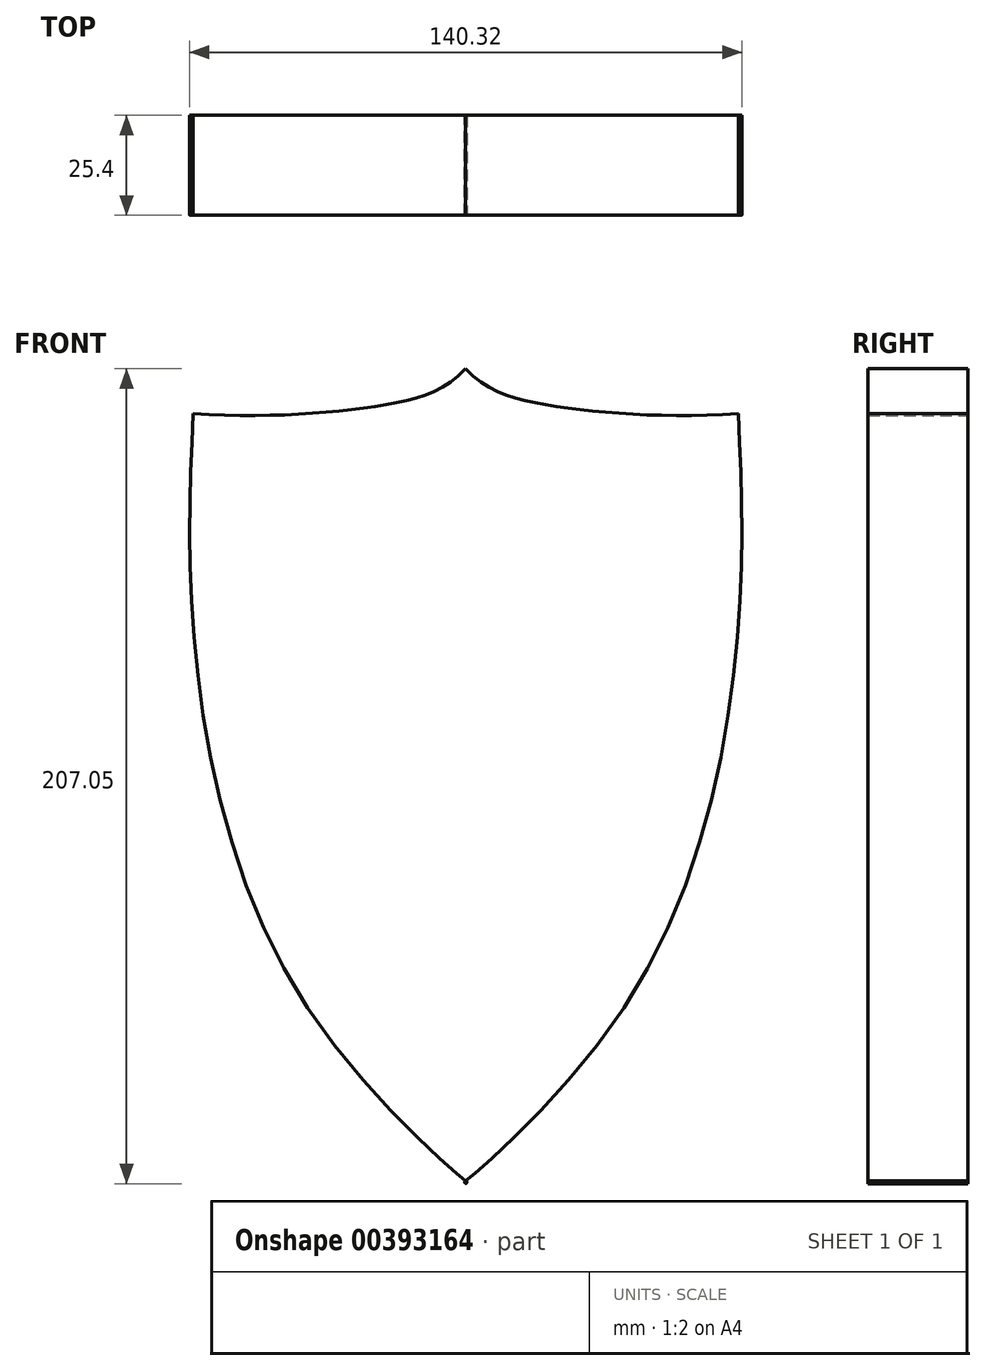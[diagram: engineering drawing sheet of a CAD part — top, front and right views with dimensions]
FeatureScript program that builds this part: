
annotation { "Feature Type Name" : "Feature", "Feature Type Description" : "" }
export const myFeature = defineFeature(function(context is Context, id is Id, definition is map)
    precondition{}
    {
        {
            var Q0;
            Q0=qCreatedBy(makeId("Front.planeOp"),FACE);
            var sketch = newSketch(context, id + "F0", { "sketchPlane" : qUnion([Q0])});
            skLineSegment(sketch, "E0.bottom", {"start": v(245.74, -123.57) * mm, "end": v(1458.6, -123.57) * mm});
            skLineSegment(sketch, "E0.top", {"start": v(239.4, -790.32) * mm, "end": v(1458.6, -790.32) * mm});
            skLineSegment(sketch, "E0.left", {"start": v(239.4, -129.92) * mm, "end": v(239.4, -790.32) * mm});
            skLineSegment(sketch, "E0.right", {"start": v(1458.6, -123.57) * mm, "end": v(1458.6, -790.32) * mm});
            skPoint(sketch, "E1.visualSharp", {"position": v(239.4, -123.57) * mm});
            skArc(sketch, "E1.filletArc", {"start": v(245.74, -123.57) * mm, "mid": v(241.25, -125.43) * mm, "end": v(239.4, -129.92) * mm});
            skLineSegment(sketch, "E2.bottom", {"start": v(331.62, -510.92) * mm, "end": v(1373.02, -510.92) * mm});
            skLineSegment(sketch, "E2.top", {"start": v(331.62, -256.92) * mm, "end": v(1373.02, -256.92) * mm});
            skLineSegment(sketch, "E2.left", {"start": v(331.62, -510.92) * mm, "end": v(331.62, -256.92) * mm});
            skLineSegment(sketch, "E2.right", {"start": v(1373.02, -510.92) * mm, "end": v(1373.02, -256.92) * mm});
            skLineSegment(sketch, "E3", {"start": v(852.32, -256.92) * mm, "end": v(852.32, -510.92) * mm});
            skLineSegment(sketch, "E4", {"start": v(239.4, -460.12) * mm, "end": v(1458.6, -460.12) * mm});
            skLineSegment(sketch, "E5", {"start": v(591.97, -256.92) * mm, "end": v(591.97, -510.92) * mm});
            skLineSegment(sketch, "E6", {"start": v(1112.67, -256.92) * mm, "end": v(1112.67, -510.92) * mm});
            skLineSegment(sketch, "E7", {"start": v(331.62, -383.92) * mm, "end": v(1373.02, -383.92) * mm});
            skLineSegment(sketch, "E8", {"start": v(387.93, -256.92) * mm, "end": v(387.93, -356.74) * mm});
            skLineSegment(sketch, "E9", {"start": v(387.93, -231.52) * mm, "end": v(1304.04, -231.52) * mm});
            skSolve(sketch);
        }
        {
            var Q0;
            Q0=qCreatedBy(makeId("Front.planeOp"),FACE);
            var sketch = newSketch(context, id + "F1", { "sketchPlane" : qUnion([Q0])});
            skFitSpline(sketch, "E10", {"points": [v(349.86, -708.02) * mm, v(374.54, -692.95) * mm, v(407.33, -686.33) * mm, v(434.74, -686.74) * mm, v(463.4, -691.51) * mm, v(471.05, -702.03) * mm, v(464.84, -718.06) * mm, v(462.86, -736.9) * mm, v(477.53, -741.07) * mm, v(490.31, -741.76) * mm, v(500.08, -742.84) * mm, v(510.45, -743.84) * mm, v(527.3, -742.85) * mm, v(530.37, -724.79) * mm, v(518.38, -715.09) * mm, v(513.42, -699.22) * mm, v(527.3, -684.35) * mm, v(611.58, -685.34) * mm, v(621.5, -702.2) * mm, v(620.5, -712.11) * mm, v(614.55, -723.02) * mm, v(618.52, -737.9) * mm, v(632.4, -744.83) * mm, v(648.26, -731.94) * mm, v(659.17, -692.28) * mm, v(689.9, -653.62) * mm, v(727.58, -643.7) * mm, v(754.35, -660.56) * mm, v(760.49, -684.85) * mm, v(761.48, -713.6) * mm, v(760.3, -726.98) * mm, v(760.27, -728.75) * mm], "startDerivative": vector(568.53, 613.84) * mm, "endDerivative": vector(-1.29, -160.05) * mm});
            skLineSegment(sketch, "E11", {"start": v(349.86, -708.02) * mm, "end": v(372.61, -715.8) * mm});
            skLineSegment(sketch, "E12", {"start": v(372.61, -715.8) * mm, "end": v(372.61, -735.76) * mm});
            skPoint(sketch, "E13.1.internal.snap0", {"position": v(372.61, -725.78) * mm});
            skPoint(sketch, "E13.4.internal.snap0", {"position": v(372.61, -725.78) * mm});
            skPoint(sketch, "E13.10.internal.snap0", {"position": v(372.61, -725.78) * mm});
            skPoint(sketch, "E13.27.internal.snap0", {"position": v(372.61, -725.78) * mm});
            skFitSpline(sketch, "E13", {"points": [v(372.61, -735.76) * mm, v(389.12, -725.78) * mm, v(407.4, -715.8) * mm, v(433.92, -715.8) * mm, v(430.98, -725.78) * mm, v(430.39, -746.98) * mm, v(501.16, -760.24) * mm, v(532.38, -758.77) * mm, v(548.39, -743.83) * mm, v(549.64, -735.76) * mm, v(545.52, -725.78) * mm, v(539.29, -715.8) * mm, v(538.24, -711.09) * mm, v(539.23, -705.51) * mm, v(586.5, -708.17) * mm, v(598.07, -718.69) * mm, v(596.32, -728.85) * mm, v(589.43, -735.76) * mm, v(599.47, -755.85) * mm, v(633.12, -766.36) * mm, v(662.92, -755.14) * mm, v(676.35, -738.27) * mm, v(684.3, -719.74) * mm, v(692.01, -695.2) * mm, v(711.3, -681.18) * mm, v(736.18, -683.28) * mm, v(746.35, -706.77) * mm, v(746.7, -725.78) * mm], "startDerivative": vector(480.76, 265.21) * mm, "endDerivative": vector(-23.41, -493.2) * mm});
            skFitSpline(sketch, "E14", {"points": [v(746.7, -725.78) * mm, v(733.74, -719.74) * mm, v(704.83, -725.78) * mm, v(698.52, -753.94) * mm, v(718.85, -772.16) * mm, v(746.7, -759.54) * mm, v(751.45, -743.77) * mm], "startDerivative": vector(-83.2, 57.25) * mm, "endDerivative": vector(8.08, 115.68) * mm});
            skFitSpline(sketch, "E15", {"points": [v(738.48, -738.16) * mm, v(718.85, -732.2) * mm, v(712.9, -742.02) * mm, v(715.7, -752.88) * mm, v(727.62, -752.88) * mm, v(738.48, -738.16) * mm]});
            skFitSpline(sketch, "E16", {"points": [v(760.27, -728.75) * mm, v(778.77, -749.1) * mm, v(786.4, -759.54) * mm, v(788.4, -770.13) * mm, v(786.4, -780.98) * mm], "startDerivative": vector(59.68, -65.07) * mm, "endDerivative": vector(-13.1, -50.07) * mm});
            skFitSpline(sketch, "E17", {"points": [v(751.45, -743.77) * mm, v(760.27, -752.86) * mm, v(755.06, -766.52) * mm, v(751.45, -781.38) * mm], "startDerivative": vector(39.46, -26.04) * mm, "endDerivative": vector(-6.05, -42.8) * mm});
            skFitSpline(sketch, "E18", {"points": [v(786.4, -780.98) * mm, v(780.3, -766.82) * mm, v(772.9, -758.58) * mm], "startDerivative": vector(-9.97, 28.37) * mm, "endDerivative": vector(-17.21, 16.09) * mm});
            skFitSpline(sketch, "E19", {"points": [v(772.9, -758.58) * mm, v(762.68, -766.82) * mm, v(751.45, -781.38) * mm], "startDerivative": vector(-49.17, -22.83) * mm, "endDerivative": vector(-38.96, -55.08) * mm});
            skFitSpline(sketch, "E20.MirrorCS", {"points": [v(944.37, -728.75) * mm, v(925.87, -749.1) * mm, v(918.24, -759.54) * mm, v(916.23, -770.13) * mm, v(918.24, -780.98) * mm], "startDerivative": vector(-59.68, -65.07) * mm, "endDerivative": vector(13.1, -50.07) * mm});
            skFitSpline(sketch, "E21.MirrorCS", {"points": [v(918.24, -780.98) * mm, v(924.34, -766.82) * mm, v(931.72, -758.58) * mm], "startDerivative": vector(9.97, 28.37) * mm, "endDerivative": vector(17.21, 16.09) * mm});
            skFitSpline(sketch, "E22.MirrorCS", {"points": [v(931.72, -758.58) * mm, v(941.95, -766.82) * mm, v(953.18, -781.38) * mm], "startDerivative": vector(49.17, -22.83) * mm, "endDerivative": vector(38.96, -55.08) * mm});
            skFitSpline(sketch, "E23.MirrorCS", {"points": [v(953.18, -743.77) * mm, v(944.37, -752.86) * mm, v(949.57, -766.52) * mm, v(953.18, -781.38) * mm], "startDerivative": vector(-39.46, -26.04) * mm, "endDerivative": vector(6.05, -42.8) * mm});
            skFitSpline(sketch, "E24.MirrorCS", {"points": [v(957.94, -725.78) * mm, v(970.9, -719.74) * mm, v(999.8, -725.78) * mm, v(1006.11, -753.94) * mm, v(985.78, -772.16) * mm, v(957.94, -759.54) * mm, v(953.18, -743.77) * mm], "startDerivative": vector(83.2, 57.25) * mm, "endDerivative": vector(-8.08, 115.68) * mm});
            skFitSpline(sketch, "E25.MirrorC", {"points": [v(966.15, -738.16) * mm, v(985.78, -732.2) * mm, v(991.74, -742.02) * mm, v(988.94, -752.88) * mm, v(977.02, -752.88) * mm, v(966.15, -738.16) * mm]});
            skFitSpline(sketch, "E26.MirrorCS", {"points": [v(1332.02, -735.76) * mm, v(1315.51, -725.78) * mm, v(1297.24, -715.8) * mm, v(1270.7, -715.8) * mm, v(1273.66, -725.78) * mm, v(1274.25, -746.98) * mm, v(1203.47, -760.24) * mm, v(1172.26, -758.77) * mm, v(1156.25, -743.83) * mm, v(1155, -735.76) * mm, v(1159.11, -725.78) * mm, v(1165.35, -715.8) * mm, v(1166.4, -711.09) * mm, v(1165.4, -705.51) * mm, v(1118.13, -708.17) * mm, v(1106.57, -718.69) * mm, v(1108.32, -728.85) * mm, v(1115.2, -735.76) * mm, v(1105.16, -755.85) * mm, v(1071.51, -766.36) * mm, v(1041.72, -755.14) * mm, v(1028.29, -738.27) * mm, v(1020.33, -719.74) * mm, v(1012.62, -695.2) * mm, v(993.34, -681.18) * mm, v(968.45, -683.28) * mm, v(958.29, -706.77) * mm, v(957.94, -725.78) * mm], "startDerivative": vector(-480.76, 265.21) * mm, "endDerivative": vector(23.41, -493.2) * mm});
            skFitSpline(sketch, "E27.MirrorCS", {"points": [v(1354.78, -708.02) * mm, v(1330.1, -692.95) * mm, v(1297.3, -686.33) * mm, v(1269.9, -686.74) * mm, v(1241.23, -691.51) * mm, v(1233.59, -702.03) * mm, v(1239.8, -718.06) * mm, v(1241.78, -736.9) * mm, v(1227.1, -741.07) * mm, v(1214.32, -741.76) * mm, v(1204.55, -742.84) * mm, v(1194.19, -743.84) * mm, v(1177.33, -742.85) * mm, v(1174.26, -724.79) * mm, v(1186.26, -715.09) * mm, v(1191.21, -699.22) * mm, v(1177.33, -684.35) * mm, v(1093.06, -685.34) * mm, v(1083.14, -702.2) * mm, v(1084.14, -712.11) * mm, v(1090.08, -723.02) * mm, v(1086.12, -737.9) * mm, v(1072.24, -744.83) * mm, v(1056.37, -731.94) * mm, v(1045.47, -692.28) * mm, v(1014.73, -653.62) * mm, v(977.06, -643.7) * mm, v(950.29, -660.56) * mm, v(944.15, -684.85) * mm, v(943.15, -713.6) * mm, v(944.34, -726.98) * mm, v(944.37, -728.75) * mm], "startDerivative": vector(-568.53, 613.84) * mm, "endDerivative": vector(1.29, -160.05) * mm});
            skLineSegment(sketch, "E28.MirrorCS", {"start": v(1354.78, -708.02) * mm, "end": v(1332.02, -715.8) * mm});
            skLineSegment(sketch, "E29.MirrorCS", {"start": v(1332.02, -715.8) * mm, "end": v(1332.02, -735.76) * mm});
            skFitSpline(sketch, "E30", {"points": [v(755.08, -627.87) * mm, v(703.73, -620.44) * mm, v(669.27, -627.2) * mm], "startDerivative": vector(-98.33, 21.37) * mm, "endDerivative": vector(-72.45, -21.4) * mm});
            skFitSpline(sketch, "E31", {"points": [v(669.27, -627.2) * mm, v(684.47, -613.34) * mm, v(715.22, -610.3) * mm], "startDerivative": vector(28.9, 36.51) * mm, "endDerivative": vector(61.88, -1.45) * mm});
            skFitSpline(sketch, "E32", {"points": [v(715.22, -610.3) * mm, v(689.9, -593.07) * mm, v(663.87, -584.96) * mm], "startDerivative": vector(-48.07, 37.8) * mm, "endDerivative": vector(-54.7, 12.63) * mm});
            skFitSpline(sketch, "E33", {"points": [v(663.87, -584.96) * mm, v(682.55, -583) * mm, v(719.77, -596.92) * mm], "startDerivative": vector(42.4, 10.59) * mm, "endDerivative": vector(67.83, -31.88) * mm});
            skFitSpline(sketch, "E34", {"points": [v(719.77, -596.92) * mm, v(721.02, -565.4) * mm, v(721.12, -564.15) * mm, v(722.62, -563.05) * mm, v(737.1, -565.4) * mm, v(749.73, -584.68) * mm, v(755.08, -627.87) * mm], "startDerivative": vector(7.9, 175.02) * mm, "endDerivative": vector(10.32, -164.76) * mm});
            skFitSpline(sketch, "E35.MirrorCS", {"points": [v(984.87, -596.92) * mm, v(983.62, -565.4) * mm, v(983.52, -564.15) * mm, v(982.01, -563.05) * mm, v(967.53, -565.4) * mm, v(954.9, -584.68) * mm, v(949.55, -627.87) * mm], "startDerivative": vector(-7.9, 175.02) * mm, "endDerivative": vector(-10.32, -164.76) * mm});
            skFitSpline(sketch, "E36.MirrorCS", {"points": [v(949.55, -627.87) * mm, v(1000.9, -620.44) * mm, v(1035.36, -627.2) * mm], "startDerivative": vector(98.33, 21.37) * mm, "endDerivative": vector(72.45, -21.4) * mm});
            skFitSpline(sketch, "E37.MirrorCS", {"points": [v(1035.36, -627.2) * mm, v(1020.16, -613.34) * mm, v(989.42, -610.3) * mm], "startDerivative": vector(-28.9, 36.51) * mm, "endDerivative": vector(-61.88, -1.45) * mm});
            skFitSpline(sketch, "E38.MirrorCS", {"points": [v(989.42, -610.3) * mm, v(1014.73, -593.07) * mm, v(1040.77, -584.96) * mm], "startDerivative": vector(48.07, 37.8) * mm, "endDerivative": vector(54.7, 12.63) * mm});
            skFitSpline(sketch, "E39.MirrorCS", {"points": [v(1040.77, -584.96) * mm, v(1022.08, -583) * mm, v(984.87, -596.92) * mm], "startDerivative": vector(-42.4, 10.59) * mm, "endDerivative": vector(-67.83, -31.88) * mm});
            skLineSegment(sketch, "E40", {"start": v(474.31, -584.06) * mm, "end": v(449.78, -609.8) * mm});
            skLineSegment(sketch, "E41", {"start": v(449.78, -609.8) * mm, "end": v(474.96, -633.8) * mm});
            skLineSegment(sketch, "E42", {"start": v(474.96, -633.8) * mm, "end": v(499.48, -607.77) * mm});
            skLineSegment(sketch, "E43", {"start": v(499.48, -607.77) * mm, "end": v(474.31, -584.06) * mm});
            skSolve(sketch);
        }
        {
            var Q0;
            Q0=qCreatedBy(makeId("Front.planeOp"),FACE);
            var sketch = newSketch(context, id + "F2", { "sketchPlane" : qUnion([Q0])});
            skLineSegment(sketch, "E44", {"start": v(852.32, -507.12) * mm, "end": v(852.32, -871.68) * mm, "construction": true});
            skFitSpline(sketch, "E45", {"points": [v(852.32, -579.1) * mm, v(830.73, -588.45) * mm, v(783.06, -590.55) * mm], "startDerivative": vector(-43.2, -44.86) * mm, "endDerivative": vector(-92.97, 6) * mm});
            skFitSpline(sketch, "E46", {"points": [v(783.06, -590.55) * mm, v(783.06, -644.53) * mm, v(811.1, -739.88) * mm, v(852.32, -785.45) * mm, v(852.32, -786.15) * mm], "startDerivative": vector(-7.96, -174.72) * mm, "endDerivative": vector(-40.78, -35.33) * mm});
            skFitSpline(sketch, "E47.MirrorCS", {"points": [v(852.32, -579.1) * mm, v(873.9, -588.45) * mm, v(921.57, -590.55) * mm], "startDerivative": vector(43.2, -44.86) * mm, "endDerivative": vector(92.97, 6) * mm});
            skFitSpline(sketch, "E48.MirrorCS", {"points": [v(921.57, -590.55) * mm, v(921.57, -644.53) * mm, v(893.53, -739.88) * mm, v(852.32, -785.45) * mm, v(852.32, -786.15) * mm], "startDerivative": vector(7.96, -174.72) * mm, "endDerivative": vector(40.78, -35.33) * mm});
            skSolve(sketch);
        }
        {
            var Q0;
            Q0 = qSketchRegion(id + "F2", true);
            extrude(context, id + "F3", {"entities" : qUnion([Q0]), "depth" : 25.4 * mm});
        }
    });
